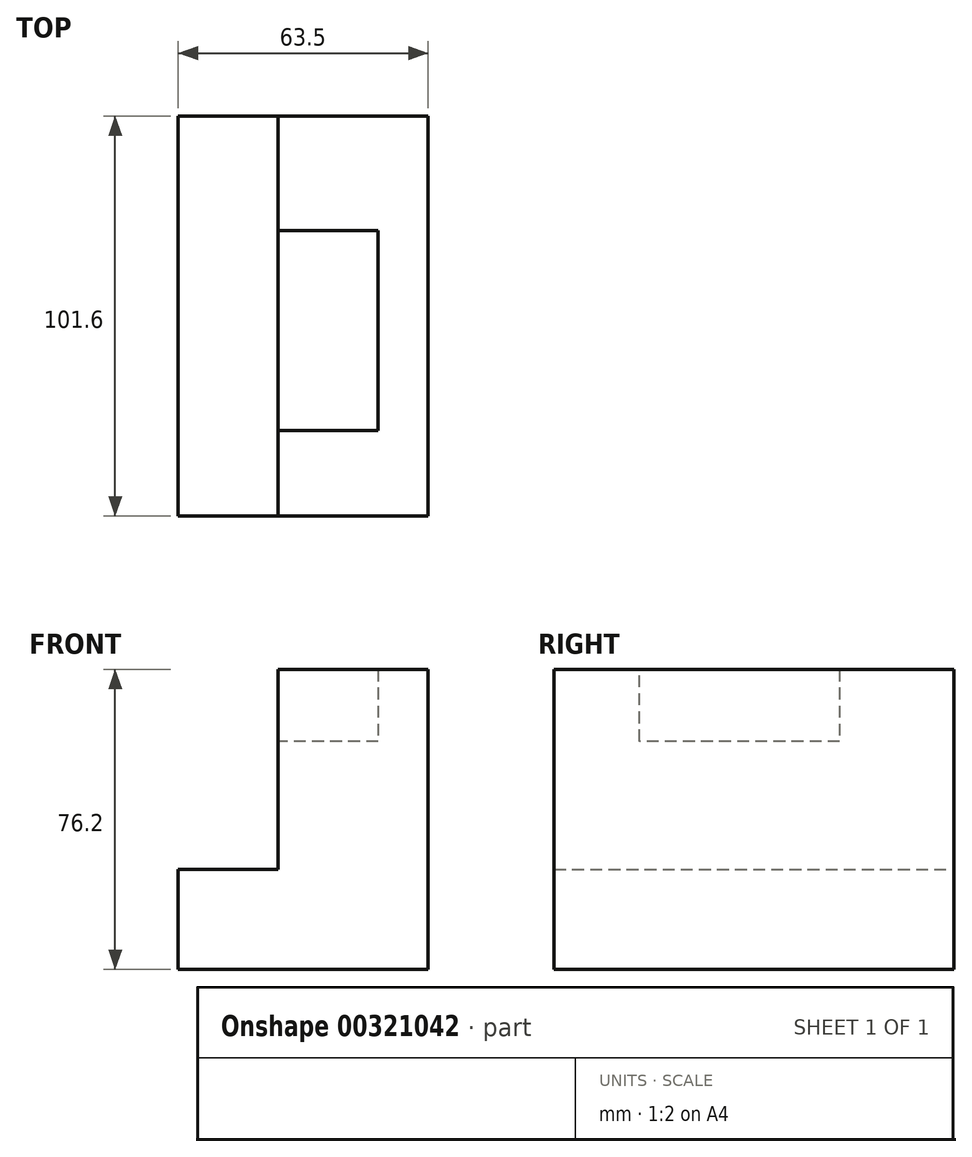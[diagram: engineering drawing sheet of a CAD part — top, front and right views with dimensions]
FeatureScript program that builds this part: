
annotation { "Feature Type Name" : "Feature", "Feature Type Description" : "" }
export const myFeature = defineFeature(function(context is Context, id is Id, definition is map)
    precondition{}
    {
        {
            var Q0;
            Q0=qCreatedBy(makeId("Front.planeOp"),FACE);
            var sketch = newSketch(context, id + "F0", { "sketchPlane" : qUnion([Q0])});
            skLineSegment(sketch, "E0", {"start": v(-46.17, -31.57) * mm, "end": v(17.33, -31.57) * mm});
            skLineSegment(sketch, "E1", {"start": v(17.33, -31.57) * mm, "end": v(17.33, 44.63) * mm});
            skLineSegment(sketch, "E2", {"start": v(17.33, 44.63) * mm, "end": v(-20.77, 44.63) * mm});
            skLineSegment(sketch, "E3", {"start": v(-20.77, 44.63) * mm, "end": v(-20.77, -6.17) * mm});
            skLineSegment(sketch, "E4", {"start": v(-20.77, -6.17) * mm, "end": v(-46.17, -6.17) * mm});
            skLineSegment(sketch, "E5", {"start": v(-46.17, -6.17) * mm, "end": v(-46.17, -31.57) * mm});
            skSolve(sketch);
        }
        {
            var Q0;
            Q0=makeQuery(id+"F0.imprint","IMPRINT",FACE,{"disambiguationData":[TD([[makeQuery(id+"F0.imprint","IMPRINT",EDGE,{"derivedFrom":sQuery(id+"F0.wireOp",EDGE,"E0")}),1.0]])]});
            extrude(context, id + "F1", {"entities" : qUnion([Q0]), "depth" : 101.6 * mm});
        }
        {
            var Q0;
            Q0=makeQuery(id+"F1.opExtrude","SWEPT_FACE",FACE,{"disambiguationData":[OSD([sQuery(id+"F0.wireOp",EDGE,"E3")])]});
            var sketch = newSketch(context, id + "F2", { "sketchPlane" : qUnion([Q0])});
            skLineSegment(sketch, "E6", {"start": v(29.07, 44.63) * mm, "end": v(29.07, 26.37) * mm});
            skLineSegment(sketch, "E7", {"start": v(29.07, 26.37) * mm, "end": v(79.87, 26.37) * mm});
            skLineSegment(sketch, "E8", {"start": v(79.87, 26.37) * mm, "end": v(79.87, 44.63) * mm});
            skSolve(sketch);
        }
        {
            var Q0;
            Q0 = qSketchRegion(id + "F2", true);
            var Q1;
            {var subQ0=sQuery(id+"F2.wireOp",EDGE,"E6");Q1=makeQuery(id+"F2.imprint","IMPRINT",FACE,{"disambiguationData":[TD([[makeQuery(id+"F2.imprint","IMPRINT",EDGE,{"derivedFrom":subQ0}),1.0]])]});}
            extrude(context, id + "F3", {"entities" : qUnion([Q0, Q1]), "operationType" : NewBodyOperationType.REMOVE, "oppositeDirection" : true, "depth" : 25.4 * mm});
        }
    });
